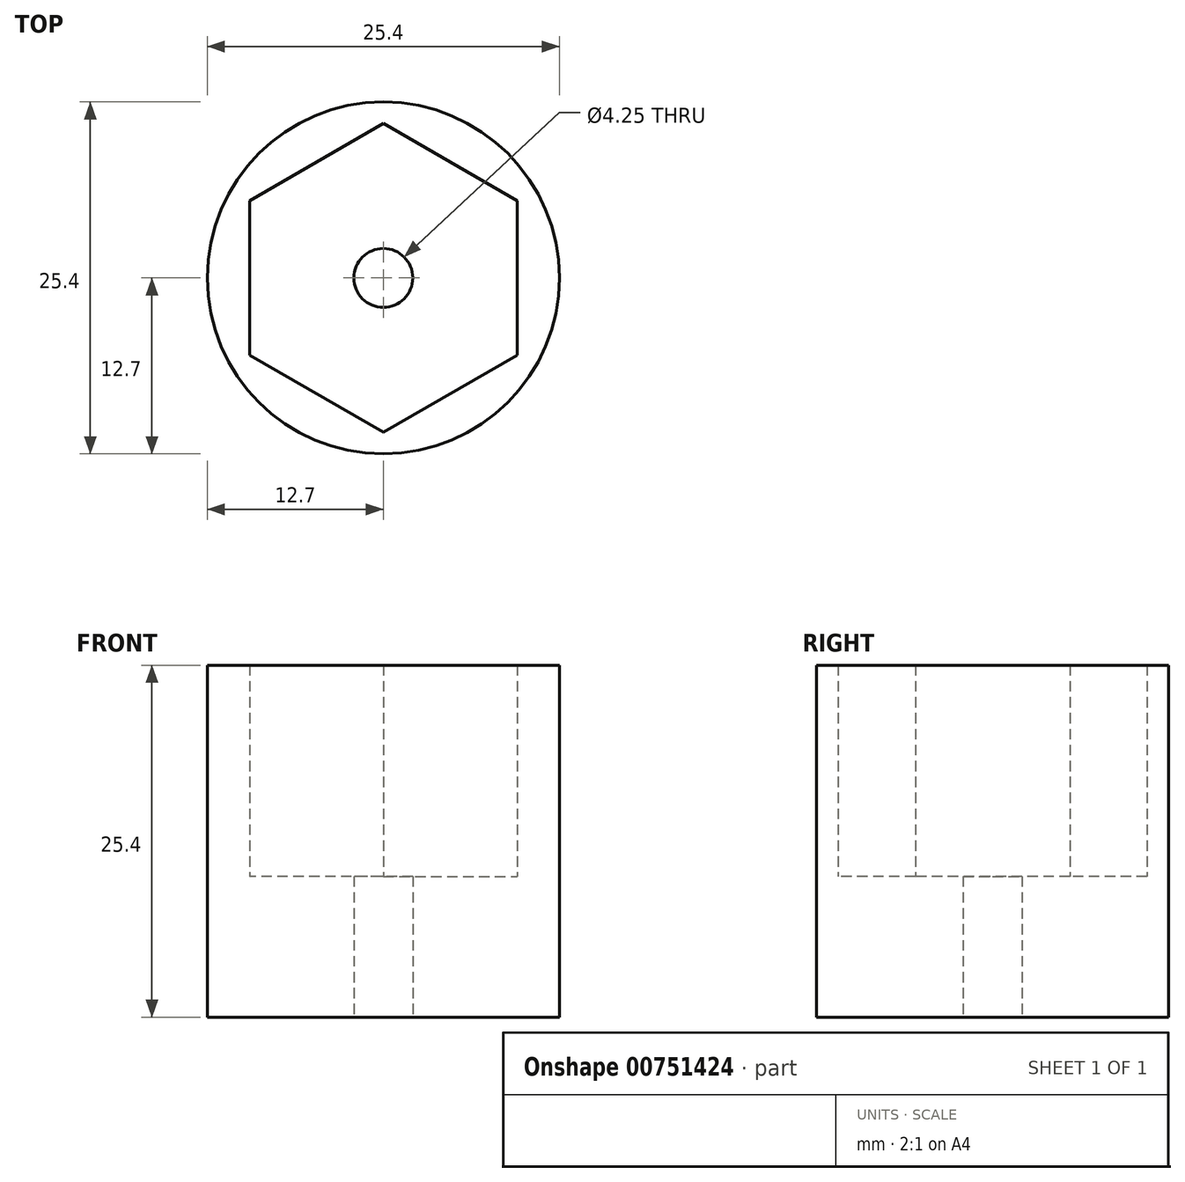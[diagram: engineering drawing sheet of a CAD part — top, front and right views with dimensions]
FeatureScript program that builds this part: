
annotation { "Feature Type Name" : "Feature", "Feature Type Description" : "" }
export const myFeature = defineFeature(function(context is Context, id is Id, definition is map)
    precondition{}
    {
        {
            var Q0;
            Q0=qCreatedBy(makeId("Top.planeOp"),FACE);
            var sketch = newSketch(context, id + "F0", { "sketchPlane" : qUnion([Q0])});
            skCircle(sketch, "E0.cCircle", {"center": v(0, 0) * mm, "radius": 9.65 * mm, "construction": true});
            skLineSegment(sketch, "E0.0", {"start": v(9.65, 5.57) * mm, "end": v(9.65, -5.57) * mm});
            skLineSegment(sketch, "E0.1", {"start": v(9.65, -5.57) * mm, "end": v(0, -11.15) * mm});
            skLineSegment(sketch, "E0.2", {"start": v(0, -11.15) * mm, "end": v(-9.65, -5.57) * mm});
            skLineSegment(sketch, "E0.3", {"start": v(-9.65, -5.57) * mm, "end": v(-9.65, 5.57) * mm});
            skLineSegment(sketch, "E0.4", {"start": v(-9.65, 5.57) * mm, "end": v(0, 11.15) * mm});
            skLineSegment(sketch, "E0.5", {"start": v(0, 11.15) * mm, "end": v(9.65, 5.57) * mm});
            skPoint(sketch, "E0.0.midPoint", {"position": v(9.65, 0) * mm});
            skCircle(sketch, "E1", {"center": v(0, 0) * mm, "radius": 2.12 * mm});
            skCircle(sketch, "E2", {"center": v(0, 0) * mm, "radius": 12.7 * mm});
            skSolve(sketch);
        }
        {
            var Q0;
            Q0=makeQuery(id+"F0.imprint","IMPRINT",FACE,{"disambiguationData":[TD([[makeQuery(id+"F0.imprint","IMPRINT",EDGE,{"derivedFrom":sQuery(id+"F0.wireOp",EDGE,"E0.0")}),1.0]])]});
            extrude(context, id + "F1", {"entities" : qUnion([Q0]), "depth" : 25.4 * mm, "offsetDistance" : 25.4 * mm});
        }
        {
            var Q0;
            Q0=makeQuery(id+"F0.imprint","IMPRINT",FACE,{"disambiguationData":[TD([[makeQuery(id+"F0.imprint","IMPRINT",EDGE,{"derivedFrom":sQuery(id+"F0.wireOp",EDGE,"E0.0")}),-1.0]])]});
            extrude(context, id + "F2", {"entities" : qUnion([Q0]), "operationType" : NewBodyOperationType.ADD, "depth" : 10.16 * mm, "offsetDistance" : 25.4 * mm});
        }
    });
